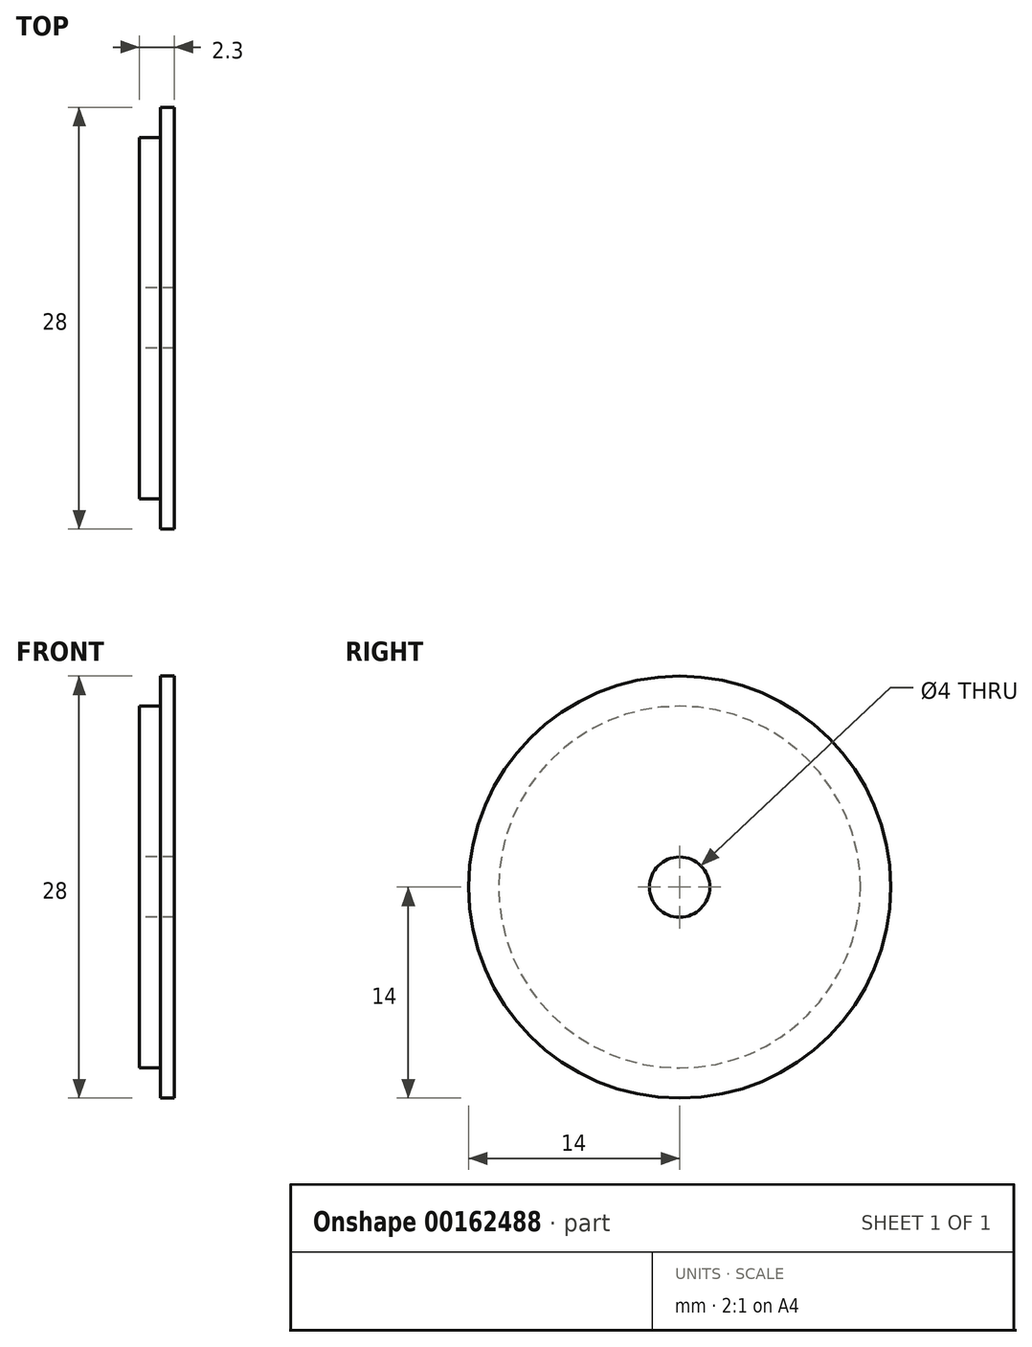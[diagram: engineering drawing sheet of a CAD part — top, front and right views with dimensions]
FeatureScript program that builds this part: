
annotation { "Feature Type Name" : "Feature", "Feature Type Description" : "" }
export const myFeature = defineFeature(function(context is Context, id is Id, definition is map)
    precondition{}
    {
        {
            var Q0;
            Q0=qCreatedBy(makeId("Top.planeOp"),FACE);
            var sketch = newSketch(context, id + "F0", { "sketchPlane" : qUnion([Q0])});
            skLineSegment(sketch, "E0", {"start": v(1.4, 12) * mm, "end": v(0, 12) * mm});
            skLineSegment(sketch, "E1", {"start": v(0, 0) * mm, "end": v(0, 14.26) * mm, "construction": true});
            skLineSegment(sketch, "E2", {"start": v(0, 0) * mm, "end": v(7.98, 0) * mm, "construction": true});
            skLineSegment(sketch, "E3", {"start": v(2.3, 2) * mm, "end": v(0, 2) * mm});
            skLineSegment(sketch, "E4", {"start": v(1.4, 12) * mm, "end": v(1.4, 14) * mm});
            skLineSegment(sketch, "E5", {"start": v(1.4, 14) * mm, "end": v(2.3, 14) * mm});
            skLineSegment(sketch, "E6", {"start": v(2.3, 14) * mm, "end": v(2.3, 2) * mm});
            skLineSegment(sketch, "E7", {"start": v(0, 12) * mm, "end": v(0, 2) * mm});
            skSolve(sketch);
        }
        {
            var Q0;
            Q0=qSketchRegion(id+"F0",true);
            var Q1;
            Q1=sQuery(id+"F0.wireOp",EDGE,"E2");
            revolve(context, id + "F1", {"entities" : qUnion([Q0]), "axis" : qUnion([Q1]), "revolveType" : RevolveType.FULL});
        }
    });
